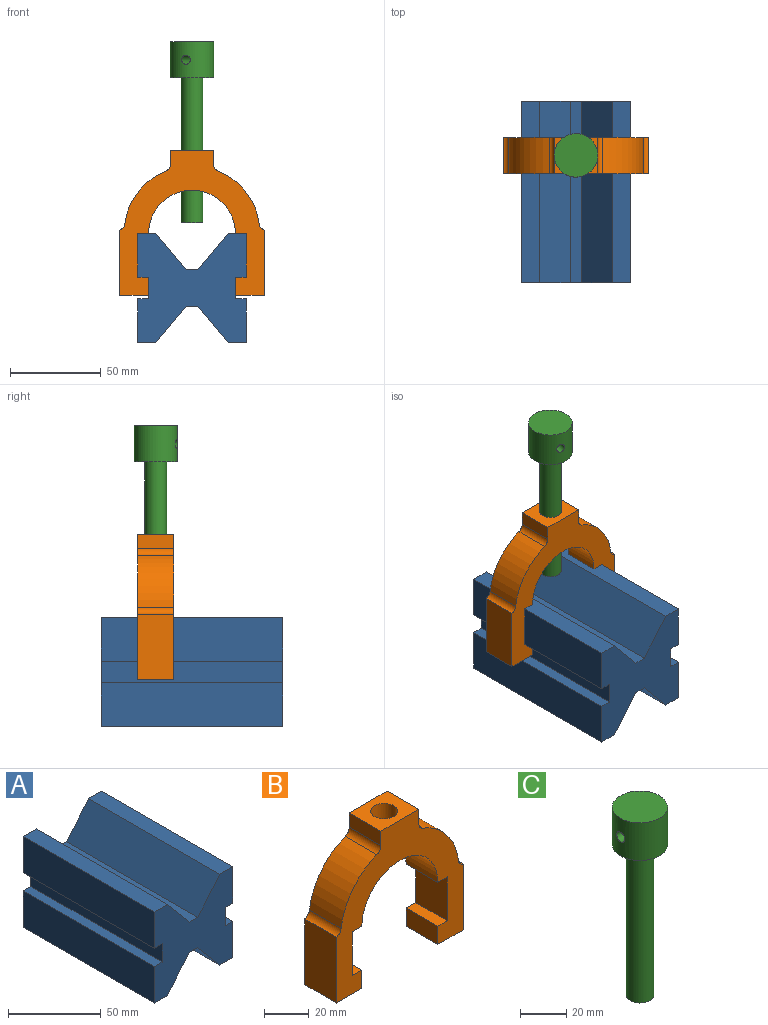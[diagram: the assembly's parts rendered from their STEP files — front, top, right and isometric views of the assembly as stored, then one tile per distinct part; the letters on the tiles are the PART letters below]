
ASSEMBLY  parts=3 mates=2
PART A: 22 faces, bbox 60x100x60 mm
  f0: plane 100x24mm, normal (1,0,0), area 2400mm2, adj f1,f19,f20,f21
  f1: plane 100x6mm, normal (0,0,1), area 600mm2, adj f0,f2,f20,f21
  f2: plane 100x12mm, normal (1,0,0), area 1200mm2, adj f1,f3,f20,f21
  f3: plane 100x6mm, normal (0,0,-1), area 600mm2, adj f2,f4,f20,f21
  f4: plane 100x24mm, normal (1,0,0), area 2400mm2, adj f3,f5,f20,f21
  f5: plane 100x9.98mm, normal (0,0,1), area 997.5mm2, adj f4,f6,f20,f21
  f6: plane 100x20mm, normal (-0.77,0,0.64), area 2610.8mm2, adj f5,f7,f20,f21
  f7: plane 100x6.49mm, normal (0,0,1), area 648.6mm2, adj f6,f8,f20,f21
  f8: plane 100x20mm, normal (0.77,0,0.64), area 2610.8mm2, adj f7,f9,f20,f21
  f9: plane 100x9.98mm, normal (0,0,1), area 997.5mm2, adj f8,f10,f20,f21
  f10: plane 100x24mm, normal (-1,0,0), area 2400mm2, adj f9,f11,f20,f21
  f11: plane 100x6mm, normal (0,0,-1), area 600mm2, adj f10,f12,f20,f21
  f12: plane 100x12mm, normal (-1,0,0), area 1200mm2, adj f11,f13,f20,f21
  f13: plane 100x6mm, normal (0,0,1), area 600mm2, adj f12,f14,f20,f21
  f14: plane 100x24mm, normal (-1,0,0), area 2400mm2, adj f13,f15,f20,f21
  f15: plane 100x9.98mm, normal (0,0,-1), area 997.5mm2, adj f14,f16,f20,f21
  f16: plane 100x20mm, normal (0.77,0,-0.64), area 2610.8mm2, adj f15,f17,f20,f21
  f17: plane 100x6.49mm, normal (0,0,-1), area 648.6mm2, adj f16,f18,f20,f21
  f18: plane 100x20mm, normal (-0.77,0,-0.64), area 2610.8mm2, adj f17,f19,f20,f21
  f19: plane 100x9.98mm, normal (0,0,-1), area 997.5mm2, adj f0,f18,f20,f21
  f20: plane 60x60mm, normal (0,1,0), area 2525.3mm2, adj f0,f1,f2,f3,f4,f5,f6,f7
  f21: plane 60x60mm, normal (0,-1,0), area 2525.3mm2, adj f0,f1,f2,f3,f4,f5,f6,f7
PART B: 25 faces, bbox 80x20x80 mm
  f0: cylinder r=36mm len=29.07mm, axis (0,1,0), area 772.4mm2, adj f1,f21,f22,f23
  f1: cylinder r=4mm len=20mm, axis (0,1,0), area 94.3mm2, adj f0,f2,f22,f23
  f2: plane 36x20mm, normal (-1,0,0), area 720mm2, adj f1,f3,f22,f23
  f3: plane 20x16mm, normal (0,0,-1), area 320mm2, adj f2,f4,f22,f23
  f4: plane 20x10mm, normal (1,0,0), area 200mm2, adj f3,f5,f22,f23
  f5: plane 20x6mm, normal (0,0,1), area 120mm2, adj f4,f6,f22,f23
  f6: plane 24x20mm, normal (1,0,0), area 480mm2, adj f5,f7,f22,f23
  f7: plane 20x6mm, normal (0,0,-1), area 120mm2, adj f6,f8,f22,f23
  f8: cylinder r=24mm len=48mm, axis (0,1,0), area 1394mm2, adj f7,f9,f22,f23,f24
  f9: plane 20x6mm, normal (0,0,-1), area 120mm2, adj f8,f10,f22,f23
  f10: plane 24x20mm, normal (-1,0,0), area 480mm2, adj f9,f11,f22,f23
  f11: plane 20x6mm, normal (0,0,1), area 120mm2, adj f10,f12,f22,f23
  f12: plane 20x10mm, normal (-1,0,0), area 200mm2, adj f11,f13,f22,f23
  f13: plane 20x16mm, normal (0,0,-1), area 320mm2, adj f12,f14,f22,f23
  f14: plane 36x20mm, normal (1,0,0), area 720mm2, adj f13,f15,f22,f23
  f15: cylinder r=4mm len=20mm, axis (0,1,0), area 94.3mm2, adj f14,f16,f22,f23
  f16: cylinder r=36mm len=29.07mm, axis (0,1,0), area 772.4mm2, adj f15,f17,f22,f23
  f17: cylinder r=4mm len=20mm, axis (0,1,0), area 95.7mm2, adj f16,f18,f22,f23
  f18: plane 20x7.84mm, normal (1,0,0), area 156.8mm2, adj f17,f19,f22,f23
  f19: plane 24x20mm, normal (0,0,1), area 366.9mm2, adj f18,f20,f22,f23,f24
  f20: plane 20x7.84mm, normal (-1,0,0), area 156.8mm2, adj f19,f21,f22,f23
  f21: cylinder r=4mm len=20mm, axis (0,1,0), area 95.7mm2, adj f0,f20,f22,f23
  f22: plane 80x80mm, normal (0,-1,0), area 2345.9mm2, adj f0,f1,f2,f3,f4,f5,f6,f7
  f23: plane 80x80mm, normal (0,1,0), area 2345.9mm2, adj f0,f1,f2,f3,f4,f5,f6,f7
  f24: cylinder r=6mm len=22.76mm, axis (0,0,1), area 843.7mm2, adj f8,f19
PART C: 6 faces, bbox 24x24x100 mm
  f0: plane 12x12mm, normal (0,0,-1), area 113.1mm2, adj f1
  f1: cylinder r=6mm len=80mm, axis (0,0,-1), area 3015.9mm2, adj f0,f2
  f2: plane 24x24mm, normal (0,0,-1), area 339.3mm2, adj f1,f3
  f3: cylinder r=12mm len=24mm, axis (0,0,-1), area 1468.4mm2, adj f2,f4,f5
  f4: plane 24x24mm, normal (0,0,1), area 452.4mm2, adj f3
  f5: cylinder r=2.5mm len=24mm, axis (1,0,0), area 372.9mm2, adj f3
PLACE A t=(14.44,-21.66,30.01)mm fixed
PLACE B t=(38.44,58.34,26.01)mm
PLACE C rot(axis=(0,0,-1),106.2deg) t=(14.44,48.34,66.01)mm
MATE slider A.f21 <-> B.f22  axis (0,-1,0) through (38.44,-21.66,36.01)mm
MATE revolute C.f1 <-> B.f24  axis (0,0,1) through (14.44,48.34,166.01)mm
